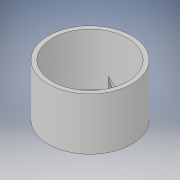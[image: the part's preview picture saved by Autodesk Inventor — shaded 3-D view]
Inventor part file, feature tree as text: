
AUTODESK INVENTOR PART (.ipt)
format: ipt  version: 2019 (Build 230136000, 136)  size: 114,688 bytes
history: native  units: mm
features: extrude x2, sketch x2
ambient origin geometry x8: Origin, YZ Plane, XZ Plane, XY Plane, X Axis, Y Axis, Z Axis, Center Point
bodies: Solid1 (feature_tree)
feature tree (4):
  extrude  "Extrusion1"  Depth=50.0mm TaperAngle=0.0deg
  extrude  "Extrusion2"  TaperAngle=15.0deg  [1 undecoded]
  sketch  "Sketch1"  dims[d1=72.0mm d2=50.0mm d3=0.0mm]
  sketch  "Sketch2"  dims[d4=30.0mm d5=0.0mm d6=15.0deg d7=15.0deg d8=80.0mm]
note: 1 required parameter value undecoded (feature->parameter linkage not recoverable at this tier; creation-order binding heuristic only, values carry confidence <= 0.55)
